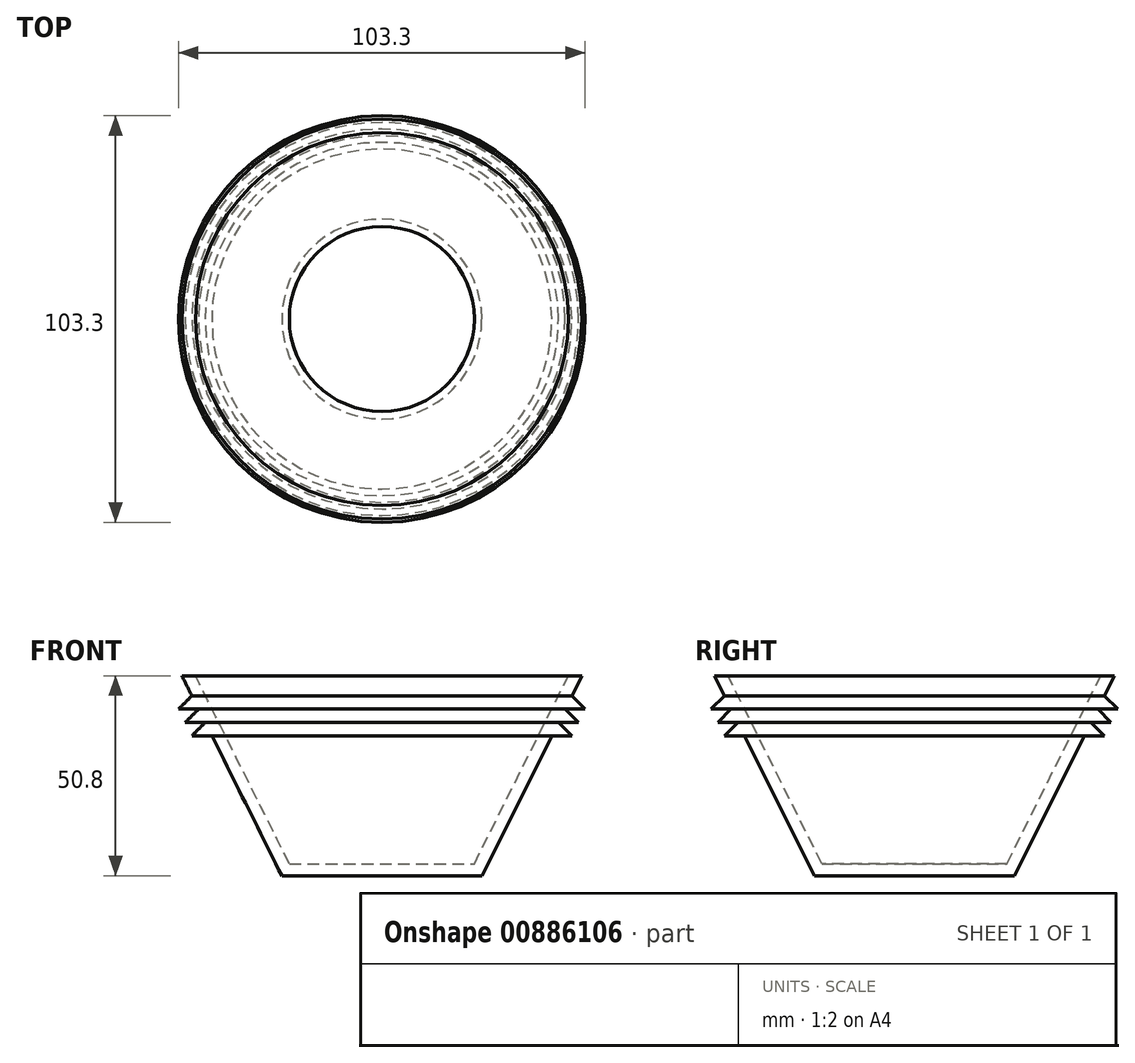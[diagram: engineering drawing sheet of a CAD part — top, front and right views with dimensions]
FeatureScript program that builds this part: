
annotation { "Feature Type Name" : "Feature", "Feature Type Description" : "" }
export const myFeature = defineFeature(function(context is Context, id is Id, definition is map)
    precondition{}
    {
        {
            var Q0;
            Q0=qCreatedBy(makeId("Front.planeOp"),FACE);
            var sketch = newSketch(context, id + "F0", { "sketchPlane" : qUnion([Q0])});
            skLineSegment(sketch, "E0", {"start": v(0, 0) * mm, "end": v(0, 50.8) * mm, "construction": true});
            skLineSegment(sketch, "E1", {"start": v(0, 0) * mm, "end": v(25.4, 0) * mm});
            skLineSegment(sketch, "E2", {"start": v(25.4, 0) * mm, "end": v(50.8, 50.8) * mm});
            skLineSegment(sketch, "E3.0", {"start": v(23.5, 3.07) * mm, "end": v(47.36, 50.8) * mm});
            skLineSegment(sketch, "E3.1", {"start": v(0, 3.07) * mm, "end": v(23.5, 3.07) * mm});
            skLineSegment(sketch, "E4", {"start": v(47.36, 50.8) * mm, "end": v(50.8, 50.8) * mm});
            skLineSegment(sketch, "E5", {"start": v(0, 3.07) * mm, "end": v(0, 0) * mm});
            skLineSegment(sketch, "E6", {"start": v(48.26, 45.72) * mm, "end": v(51.65, 42.33) * mm});
            skLineSegment(sketch, "E7", {"start": v(51.65, 42.33) * mm, "end": v(46.57, 42.33) * mm});
            skLineSegment(sketch, "E8", {"start": v(46.57, 42.33) * mm, "end": v(49.95, 38.95) * mm});
            skLineSegment(sketch, "E9", {"start": v(49.95, 38.95) * mm, "end": v(44.87, 38.95) * mm});
            skLineSegment(sketch, "E10", {"start": v(44.87, 38.95) * mm, "end": v(48.26, 35.56) * mm});
            skLineSegment(sketch, "E11", {"start": v(48.26, 35.56) * mm, "end": v(43.18, 35.56) * mm});
            skSolve(sketch);
        }
        {
            var Q0;
            Q0=makeQuery(id+"F0.imprint","IMPRINT",FACE,{"disambiguationData":[TD([[makeQuery(id+"F0.imprint","IMPRINT",EDGE,{"derivedFrom":sQuery(id+"F0.wireOp",EDGE,"E1")}),1.0]])]});
            var Q1;
            {var subQ0=sQuery(id+"F0.wireOp",EDGE,"E6");Q1=makeQuery(id+"F0.imprint","IMPRINT",FACE,{"disambiguationData":[TD([[makeQuery(id+"F0.imprint","IMPRINT",EDGE,{"derivedFrom":subQ0}),-1.0]])]});}
            var Q2;
            {var subQ0=sQuery(id+"F0.wireOp",EDGE,"E8");Q2=makeQuery(id+"F0.imprint","IMPRINT",FACE,{"disambiguationData":[TD([[makeQuery(id+"F0.imprint","IMPRINT",EDGE,{"derivedFrom":subQ0}),-1.0]])]});}
            var Q3;
            {var subQ0=sQuery(id+"F0.wireOp",EDGE,"E10");Q3=makeQuery(id+"F0.imprint","IMPRINT",FACE,{"disambiguationData":[TD([[makeQuery(id+"F0.imprint","IMPRINT",EDGE,{"derivedFrom":subQ0}),-1.0]])]});}
            var Q4;
            Q4=sQuery(id+"F0.wireOp",EDGE,"E0");
            revolve(context, id + "F1", {"surfaceOperationType" : NewSurfaceOperationType.NEW, "entities" : qUnion([Q0, Q1, Q2, Q3]), "axis" : qUnion([Q4]), "revolveType" : RevolveType.FULL});
        }
    });
